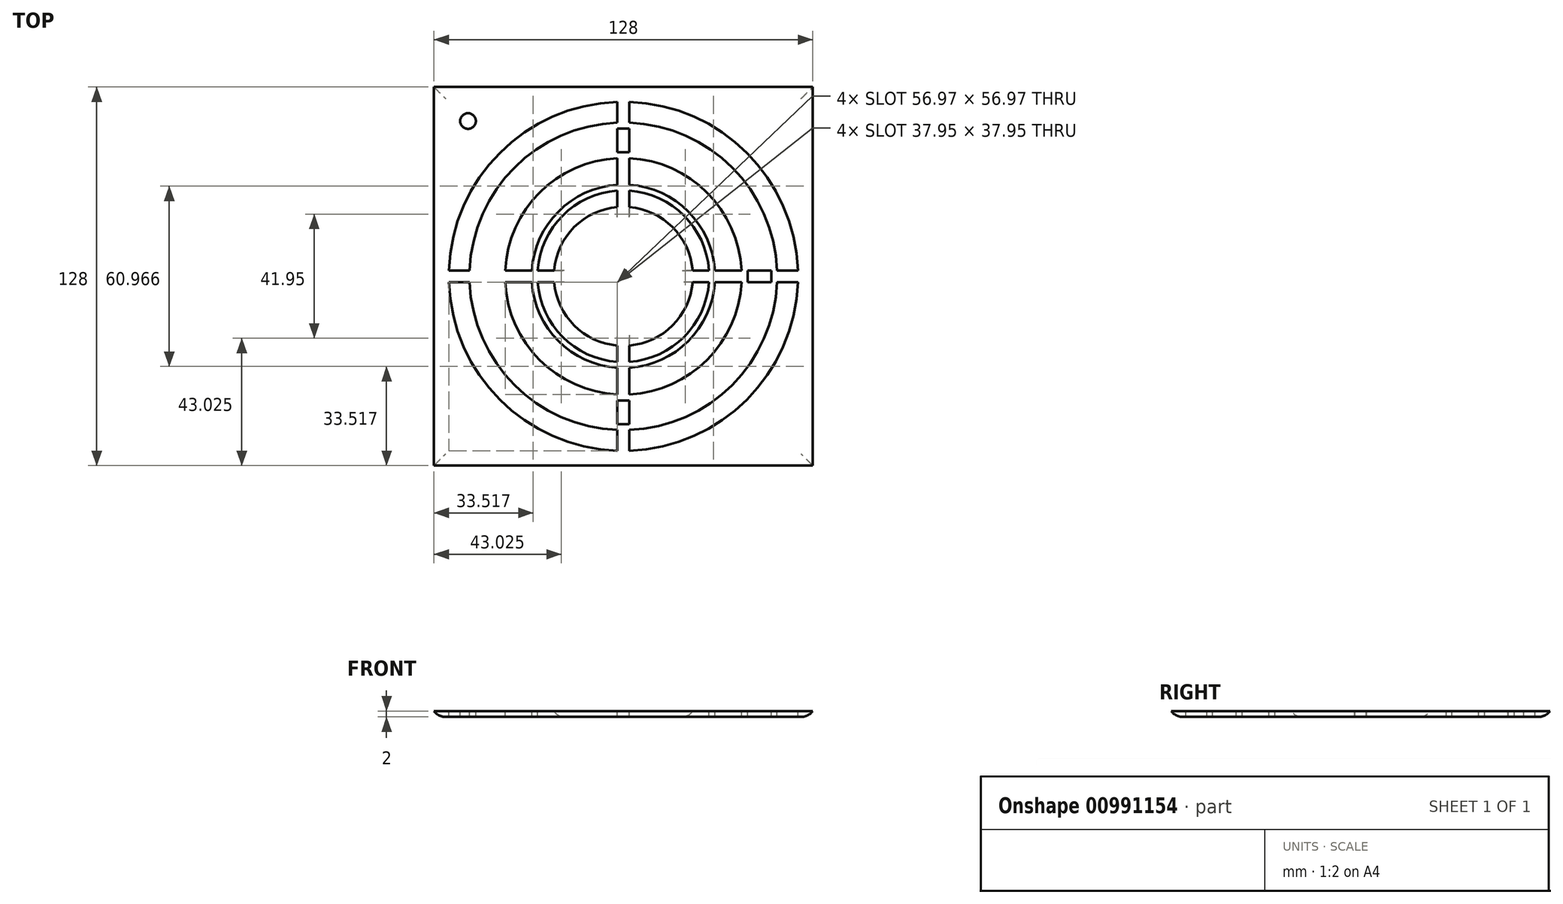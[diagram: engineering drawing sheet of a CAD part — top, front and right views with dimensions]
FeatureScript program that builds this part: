
annotation { "Feature Type Name" : "Feature", "Feature Type Description" : "" }
export const myFeature = defineFeature(function(context is Context, id is Id, definition is map)
    precondition{}
    {
        {
            var Q0;
            Q0=qCreatedBy(makeId("Top.planeOp"),FACE);
            var sketch = newSketch(context, id + "F0", { "sketchPlane" : qUnion([Q0])});
            skLineSegment(sketch, "E0.bottom", {"start": v(-64, 64) * mm, "end": v(64, 64) * mm});
            skLineSegment(sketch, "E0.top", {"start": v(-64, -64) * mm, "end": v(64, -64) * mm});
            skLineSegment(sketch, "E0.left", {"start": v(-64, 64) * mm, "end": v(-64, -64) * mm});
            skLineSegment(sketch, "E0.right", {"start": v(64, 64) * mm, "end": v(64, -64) * mm});
            skSolve(sketch);
        }
        {
            var Q0;
            Q0=makeQuery(id+"F0.imprint","IMPRINT",FACE,{"disambiguationData":[TD([[makeQuery(id+"F0.imprint","IMPRINT",EDGE,{"derivedFrom":sQuery(id+"F0.wireOp",EDGE,"E0.bottom")}),-1.0]])]});
            extrude(context, id + "F1", {"entities" : qUnion([Q0]), "depth" : 2 * mm, "offsetDistance" : 25 * mm});
        }
        {
            var Q0;
            Q0=makeQuery(id+"F1.opExtrude","CAP_FACE",FACE,{"disambiguationData":[OSD([sQuery(id+"F0.wireOp",EDGE,"E0.bottom"),sQuery(id+"F0.wireOp",EDGE,"E0.top"),sQuery(id+"F0.wireOp",EDGE,"E0.left"),sQuery(id+"F0.wireOp",EDGE,"E0.right")])],"isStart":false});
            var sketch = newSketch(context, id + "F2", { "sketchPlane" : qUnion([Q0])});
            skCircle(sketch, "E1", {"center": v(0, 0) * mm, "radius": 59 * mm});
            skCircle(sketch, "E2", {"center": v(0, 0) * mm, "radius": 23.5 * mm});
            skLineSegment(sketch, "E3", {"start": v(58.35, -64) * mm, "end": v(64, -58.35) * mm});
            skCircle(sketch, "E4", {"center": v(0, 0) * mm, "radius": 52 * mm});
            skCircle(sketch, "E5", {"center": v(0, 0) * mm, "radius": 50 * mm});
            skCircle(sketch, "E6", {"center": v(0, 0) * mm, "radius": 42 * mm});
            skCircle(sketch, "E7", {"center": v(0, 0) * mm, "radius": 40 * mm});
            skCircle(sketch, "E8", {"center": v(0, 0) * mm, "radius": 31 * mm});
            skCircle(sketch, "E9", {"center": v(0, 0) * mm, "radius": 29 * mm});
            skLineSegment(sketch, "E10.bottom", {"start": v(-2, -64) * mm, "end": v(2, -64) * mm});
            skLineSegment(sketch, "E10.top", {"start": v(-2, 64) * mm, "end": v(2, 64) * mm});
            skLineSegment(sketch, "E10.left", {"start": v(-2, -64) * mm, "end": v(-2, 64) * mm});
            skLineSegment(sketch, "E10.right", {"start": v(2, -64) * mm, "end": v(2, 64) * mm});
            skLineSegment(sketch, "E11.bottom", {"start": v(64, 2) * mm, "end": v(-64, 2) * mm});
            skLineSegment(sketch, "E11.top", {"start": v(64, -2) * mm, "end": v(-64, -2) * mm});
            skLineSegment(sketch, "E11.left", {"start": v(64, 2) * mm, "end": v(64, -2) * mm});
            skLineSegment(sketch, "E11.right", {"start": v(-64, 2) * mm, "end": v(-64, -2) * mm});
            skSolve(sketch);
        }
        {
            var Q0;
            {var subQ0=sQuery(id+"F2.wireOp",EDGE,"E10.right");var subQ1=sQuery(id+"F2.wireOp",EDGE,"E1");var subQ2=makeQuery(id+"F2.imprint","INTERSECT",VERTEX,{"disambiguationData":[OD(0.0)],"derivedFrom":[subQ1,subQ0]});Q0=makeQuery(id+"F2.imprint","IMPRINT",FACE,{"disambiguationData":[TD([[makeQuery(id+"F2.imprint","IMPRINT",EDGE,{"disambiguationData":[TD([[subQ2,1.0]])],"derivedFrom":subQ1}),1.0]])]});}
            var Q1;
            {var subQ0=sQuery(id+"F2.wireOp",EDGE,"E10.right");var subQ1=sQuery(id+"F2.wireOp",EDGE,"E5");var subQ2=makeQuery(id+"F2.imprint","INTERSECT",VERTEX,{"disambiguationData":[OD(0.0)],"derivedFrom":[subQ1,subQ0]});Q1=makeQuery(id+"F2.imprint","IMPRINT",FACE,{"disambiguationData":[TD([[makeQuery(id+"F2.imprint","IMPRINT",EDGE,{"disambiguationData":[TD([[subQ2,1.0]])],"derivedFrom":subQ1}),1.0]])]});}
            var Q2;
            {var subQ0=sQuery(id+"F2.wireOp",EDGE,"E10.right");var subQ1=sQuery(id+"F2.wireOp",EDGE,"E7");var subQ2=makeQuery(id+"F2.imprint","INTERSECT",VERTEX,{"disambiguationData":[OD(0.0)],"derivedFrom":[subQ1,subQ0]});Q2=makeQuery(id+"F2.imprint","IMPRINT",FACE,{"disambiguationData":[TD([[makeQuery(id+"F2.imprint","IMPRINT",EDGE,{"disambiguationData":[TD([[subQ2,1.0]])],"derivedFrom":subQ1}),1.0]])]});}
            var Q3;
            {var subQ0=sQuery(id+"F2.wireOp",EDGE,"E10.right");var subQ1=sQuery(id+"F2.wireOp",EDGE,"E2");var subQ2=makeQuery(id+"F2.imprint","INTERSECT",VERTEX,{"disambiguationData":[OD(0.0)],"derivedFrom":[subQ1,subQ0]});Q3=makeQuery(id+"F2.imprint","IMPRINT",FACE,{"disambiguationData":[TD([[makeQuery(id+"F2.imprint","IMPRINT",EDGE,{"disambiguationData":[TD([[subQ2,1.0]])],"derivedFrom":subQ1}),-1.0]])]});}
            var Q4;
            {var subQ0=sQuery(id+"F2.wireOp",EDGE,"E10.right");var subQ1=sQuery(id+"F2.wireOp",EDGE,"E2");var subQ2=makeQuery(id+"F2.imprint","INTERSECT",VERTEX,{"disambiguationData":[OD(1.0)],"derivedFrom":[subQ1,subQ0]});Q4=makeQuery(id+"F2.imprint","IMPRINT",FACE,{"disambiguationData":[TD([[makeQuery(id+"F2.imprint","IMPRINT",EDGE,{"disambiguationData":[TD([[subQ2,-1.0]])],"derivedFrom":subQ1}),-1.0]])]});}
            var Q5;
            {var subQ0=sQuery(id+"F2.wireOp",EDGE,"E10.right");var subQ1=sQuery(id+"F2.wireOp",EDGE,"E7");var subQ2=makeQuery(id+"F2.imprint","INTERSECT",VERTEX,{"disambiguationData":[OD(1.0)],"derivedFrom":[subQ1,subQ0]});Q5=makeQuery(id+"F2.imprint","IMPRINT",FACE,{"disambiguationData":[TD([[makeQuery(id+"F2.imprint","IMPRINT",EDGE,{"disambiguationData":[TD([[subQ2,-1.0]])],"derivedFrom":subQ1}),1.0]])]});}
            var Q6;
            {var subQ0=sQuery(id+"F2.wireOp",EDGE,"E10.right");var subQ1=sQuery(id+"F2.wireOp",EDGE,"E5");var subQ2=makeQuery(id+"F2.imprint","INTERSECT",VERTEX,{"disambiguationData":[OD(1.0)],"derivedFrom":[subQ1,subQ0]});Q6=makeQuery(id+"F2.imprint","IMPRINT",FACE,{"disambiguationData":[TD([[makeQuery(id+"F2.imprint","IMPRINT",EDGE,{"disambiguationData":[TD([[subQ2,-1.0]])],"derivedFrom":subQ1}),1.0]])]});}
            var Q7;
            {var subQ0=sQuery(id+"F2.wireOp",EDGE,"E10.right");var subQ1=sQuery(id+"F2.wireOp",EDGE,"E1");var subQ2=makeQuery(id+"F2.imprint","INTERSECT",VERTEX,{"disambiguationData":[OD(1.0)],"derivedFrom":[subQ1,subQ0]});Q7=makeQuery(id+"F2.imprint","IMPRINT",FACE,{"disambiguationData":[TD([[makeQuery(id+"F2.imprint","IMPRINT",EDGE,{"disambiguationData":[TD([[subQ2,-1.0]])],"derivedFrom":subQ1}),1.0]])]});}
            var Q8;
            {var subQ0=sQuery(id+"F2.wireOp",EDGE,"E11.top");var subQ1=sQuery(id+"F2.wireOp",EDGE,"E2");var subQ2=makeQuery(id+"F2.imprint","INTERSECT",VERTEX,{"disambiguationData":[OD(0.0)],"derivedFrom":[subQ1,subQ0]});Q8=makeQuery(id+"F2.imprint","IMPRINT",FACE,{"disambiguationData":[TD([[makeQuery(id+"F2.imprint","IMPRINT",EDGE,{"disambiguationData":[TD([[subQ2,-1.0]])],"derivedFrom":subQ1}),-1.0]])]});}
            var Q9;
            {var subQ0=sQuery(id+"F2.wireOp",EDGE,"E11.top");var subQ1=sQuery(id+"F2.wireOp",EDGE,"E7");var subQ2=makeQuery(id+"F2.imprint","INTERSECT",VERTEX,{"disambiguationData":[OD(0.0)],"derivedFrom":[subQ1,subQ0]});Q9=makeQuery(id+"F2.imprint","IMPRINT",FACE,{"disambiguationData":[TD([[makeQuery(id+"F2.imprint","IMPRINT",EDGE,{"disambiguationData":[TD([[subQ2,-1.0]])],"derivedFrom":subQ1}),1.0]])]});}
            var Q10;
            {var subQ0=sQuery(id+"F2.wireOp",EDGE,"E11.top");var subQ1=sQuery(id+"F2.wireOp",EDGE,"E5");var subQ2=makeQuery(id+"F2.imprint","INTERSECT",VERTEX,{"disambiguationData":[OD(0.0)],"derivedFrom":[subQ1,subQ0]});Q10=makeQuery(id+"F2.imprint","IMPRINT",FACE,{"disambiguationData":[TD([[makeQuery(id+"F2.imprint","IMPRINT",EDGE,{"disambiguationData":[TD([[subQ2,-1.0]])],"derivedFrom":subQ1}),1.0]])]});}
            var Q11;
            {var subQ0=sQuery(id+"F2.wireOp",EDGE,"E11.top");var subQ1=sQuery(id+"F2.wireOp",EDGE,"E1");var subQ2=makeQuery(id+"F2.imprint","INTERSECT",VERTEX,{"disambiguationData":[OD(0.0)],"derivedFrom":[subQ1,subQ0]});Q11=makeQuery(id+"F2.imprint","IMPRINT",FACE,{"disambiguationData":[TD([[makeQuery(id+"F2.imprint","IMPRINT",EDGE,{"disambiguationData":[TD([[subQ2,-1.0]])],"derivedFrom":subQ1}),1.0]])]});}
            var Q12;
            {var subQ0=sQuery(id+"F2.wireOp",EDGE,"E10.left");var subQ1=sQuery(id+"F2.wireOp",EDGE,"E2");var subQ2=makeQuery(id+"F2.imprint","INTERSECT",VERTEX,{"disambiguationData":[OD(0.0)],"derivedFrom":[subQ1,subQ0]});Q12=makeQuery(id+"F2.imprint","IMPRINT",FACE,{"disambiguationData":[TD([[makeQuery(id+"F2.imprint","IMPRINT",EDGE,{"disambiguationData":[TD([[subQ2,-1.0]])],"derivedFrom":subQ1}),-1.0]])]});}
            var Q13;
            {var subQ0=sQuery(id+"F2.wireOp",EDGE,"E10.left");var subQ1=sQuery(id+"F2.wireOp",EDGE,"E7");var subQ2=makeQuery(id+"F2.imprint","INTERSECT",VERTEX,{"disambiguationData":[OD(0.0)],"derivedFrom":[subQ1,subQ0]});Q13=makeQuery(id+"F2.imprint","IMPRINT",FACE,{"disambiguationData":[TD([[makeQuery(id+"F2.imprint","IMPRINT",EDGE,{"disambiguationData":[TD([[subQ2,-1.0]])],"derivedFrom":subQ1}),1.0]])]});}
            var Q14;
            {var subQ0=sQuery(id+"F2.wireOp",EDGE,"E10.left");var subQ1=sQuery(id+"F2.wireOp",EDGE,"E5");var subQ2=makeQuery(id+"F2.imprint","INTERSECT",VERTEX,{"disambiguationData":[OD(0.0)],"derivedFrom":[subQ1,subQ0]});Q14=makeQuery(id+"F2.imprint","IMPRINT",FACE,{"disambiguationData":[TD([[makeQuery(id+"F2.imprint","IMPRINT",EDGE,{"disambiguationData":[TD([[subQ2,-1.0]])],"derivedFrom":subQ1}),1.0]])]});}
            var Q15;
            {var subQ0=sQuery(id+"F2.wireOp",EDGE,"E10.left");var subQ1=sQuery(id+"F2.wireOp",EDGE,"E1");var subQ2=makeQuery(id+"F2.imprint","INTERSECT",VERTEX,{"disambiguationData":[OD(0.0)],"derivedFrom":[subQ1,subQ0]});Q15=makeQuery(id+"F2.imprint","IMPRINT",FACE,{"disambiguationData":[TD([[makeQuery(id+"F2.imprint","IMPRINT",EDGE,{"disambiguationData":[TD([[subQ2,-1.0]])],"derivedFrom":subQ1}),1.0]])]});}
            extrude(context, id + "F3", {"entities" : qUnion([Q0, Q1, Q2, Q3, Q4, Q5, Q6, Q7, Q8, Q9, Q10, Q11, Q12, Q13, Q14, Q15]), "operationType" : NewBodyOperationType.REMOVE, "oppositeDirection" : true, "depth" : 25 * mm, "offsetDistance" : 25 * mm});
        }
        {
            var Q0;
            Q0=makeQuery(id+"F1.opExtrude","CAP_FACE",FACE,{"disambiguationData":[OSD([sQuery(id+"F0.wireOp",EDGE,"E0.bottom"),sQuery(id+"F0.wireOp",EDGE,"E0.top"),sQuery(id+"F0.wireOp",EDGE,"E0.left"),sQuery(id+"F0.wireOp",EDGE,"E0.right")])],"isStart":false});
            var sketch = newSketch(context, id + "F4", { "sketchPlane" : qUnion([Q0])});
            skCircle(sketch, "E12", {"center": v(-52.5, 52.5) * mm, "radius": 2.65 * mm});
            skSolve(sketch);
        }
        {
            var Q0;
            Q0=makeQuery(id+"F4.imprint","IMPRINT",FACE,{"disambiguationData":[TD([[makeQuery(id+"F4.imprint","IMPRINT",EDGE,{"derivedFrom":sQuery(id+"F4.wireOp",EDGE,"E12")}),1.0]])]});
            var Q1;
            Q1=makeQuery(id+"FDiSF2rHMs3ckj9_1.1.F4.imprint","IMPRINT",FACE,{"disambiguationData":[TD([[makeQuery(id+"FDiSF2rHMs3ckj9_1.1.F4.imprint","IMPRINT",EDGE,{"derivedFrom":sQuery(id+"FDiSF2rHMs3ckj9_1.1.F4.wireOp",EDGE,"E12")}),1.0]])]});
            var Q2;
            Q2=makeQuery(id+"F1f606Lsx4S6UX4_1.1.FDiSF2rHMs3ckj9_1.1.F4.imprint","IMPRINT",FACE,{"disambiguationData":[TD([[makeQuery(id+"F1f606Lsx4S6UX4_1.1.FDiSF2rHMs3ckj9_1.1.F4.imprint","IMPRINT",EDGE,{"derivedFrom":sQuery(id+"F1f606Lsx4S6UX4_1.1.FDiSF2rHMs3ckj9_1.1.F4.wireOp",EDGE,"E12")}),1.0]])]});
            var Q3;
            Q3=makeQuery(id+"F1f606Lsx4S6UX4_1.1.F4.imprint","IMPRINT",FACE,{"disambiguationData":[TD([[makeQuery(id+"F1f606Lsx4S6UX4_1.1.F4.imprint","IMPRINT",EDGE,{"derivedFrom":sQuery(id+"F1f606Lsx4S6UX4_1.1.F4.wireOp",EDGE,"E12")}),1.0]])]});
            extrude(context, id + "F5", {"entities" : qUnion([Q0, Q1, Q2, Q3]), "operationType" : NewBodyOperationType.REMOVE, "oppositeDirection" : true, "depth" : 25 * mm, "offsetDistance" : 25 * mm});
        }
        {
            var Q0;
            Q0=makeQuery(id+"F1.opExtrude","CAP_EDGE",EDGE,{"disambiguationData":[OSD([sQuery(id+"F0.wireOp",EDGE,"E0.top")])],"isStart":true});
            var Q1;
            Q1=makeQuery(id+"F1.opExtrude","CAP_EDGE",EDGE,{"disambiguationData":[OSD([sQuery(id+"F0.wireOp",EDGE,"E0.left")])],"isStart":true});
            var Q2;
            Q2=makeQuery(id+"F1.opExtrude","CAP_EDGE",EDGE,{"disambiguationData":[OSD([sQuery(id+"F0.wireOp",EDGE,"E0.bottom")])],"isStart":true});
            var Q3;
            Q3=makeQuery(id+"F1.opExtrude","CAP_EDGE",EDGE,{"disambiguationData":[OSD([sQuery(id+"F0.wireOp",EDGE,"E0.right")])],"isStart":true});
            fillet(context, id + "F6", {"entities" : qUnion([Q0, Q1, Q2, Q3]), "radius" : 5 * mm, "tangentPropagation" : true, "allowEdgeOverflow" : false});
        }
        {
            var Q0;
            {var subQ0=sQuery(id+"F2.wireOp",EDGE,"E2");Q0=makeQuery(id+"F3.boolean.opBoolean","INTERSECT",EDGE,{"derivedFrom":[makeQuery(id+"F1.opExtrude","CAP_FACE",FACE,{"disambiguationData":[OSD([sQuery(id+"F0.wireOp",EDGE,"E0.bottom"),sQuery(id+"F0.wireOp",EDGE,"E0.top"),sQuery(id+"F0.wireOp",EDGE,"E0.left"),sQuery(id+"F0.wireOp",EDGE,"E0.right")])],"isStart":true}),makeQuery(id+"F3.opExtrude","SWEPT_FACE",FACE,{"disambiguationData":[OSD([subQ0]),TDD([makeQuery(id+"F2.imprint","IMPRINT",EDGE,{"disambiguationData":[TD([[makeQuery(id+"F2.imprint","INTERSECT",VERTEX,{"disambiguationData":[OD(0.0)],"derivedFrom":[subQ0,sQuery(id+"F2.wireOp",EDGE,"E10.left")]}),-1.0]])],"derivedFrom":subQ0})])]})]});}
            var Q1;
            {var subQ0=sQuery(id+"F2.wireOp",EDGE,"E2");Q1=makeQuery(id+"F3.boolean.opBoolean","INTERSECT",EDGE,{"derivedFrom":[makeQuery(id+"F1.opExtrude","CAP_FACE",FACE,{"disambiguationData":[OSD([sQuery(id+"F0.wireOp",EDGE,"E0.bottom"),sQuery(id+"F0.wireOp",EDGE,"E0.top"),sQuery(id+"F0.wireOp",EDGE,"E0.left"),sQuery(id+"F0.wireOp",EDGE,"E0.right")])],"isStart":true}),makeQuery(id+"F3.opExtrude","SWEPT_FACE",FACE,{"disambiguationData":[OSD([subQ0]),TDD([makeQuery(id+"F2.imprint","IMPRINT",EDGE,{"disambiguationData":[TD([[makeQuery(id+"F2.imprint","INTERSECT",VERTEX,{"disambiguationData":[OD(0.0)],"derivedFrom":[subQ0,sQuery(id+"F2.wireOp",EDGE,"E10.right")]}),1.0]])],"derivedFrom":subQ0})])]})]});}
            var Q2;
            {var subQ0=sQuery(id+"F2.wireOp",EDGE,"E2");Q2=makeQuery(id+"F3.boolean.opBoolean","INTERSECT",EDGE,{"derivedFrom":[makeQuery(id+"F1.opExtrude","CAP_FACE",FACE,{"disambiguationData":[OSD([sQuery(id+"F0.wireOp",EDGE,"E0.bottom"),sQuery(id+"F0.wireOp",EDGE,"E0.top"),sQuery(id+"F0.wireOp",EDGE,"E0.left"),sQuery(id+"F0.wireOp",EDGE,"E0.right")])],"isStart":true}),makeQuery(id+"F3.opExtrude","SWEPT_FACE",FACE,{"disambiguationData":[OSD([subQ0]),TDD([makeQuery(id+"F2.imprint","IMPRINT",EDGE,{"disambiguationData":[TD([[makeQuery(id+"F2.imprint","INTERSECT",VERTEX,{"disambiguationData":[OD(1.0)],"derivedFrom":[subQ0,sQuery(id+"F2.wireOp",EDGE,"E10.right")]}),-1.0]])],"derivedFrom":subQ0})])]})]});}
            var Q3;
            {var subQ0=sQuery(id+"F2.wireOp",EDGE,"E2");Q3=makeQuery(id+"F3.boolean.opBoolean","INTERSECT",EDGE,{"derivedFrom":[makeQuery(id+"F1.opExtrude","CAP_FACE",FACE,{"disambiguationData":[OSD([sQuery(id+"F0.wireOp",EDGE,"E0.bottom"),sQuery(id+"F0.wireOp",EDGE,"E0.top"),sQuery(id+"F0.wireOp",EDGE,"E0.left"),sQuery(id+"F0.wireOp",EDGE,"E0.right")])],"isStart":true}),makeQuery(id+"F3.opExtrude","SWEPT_FACE",FACE,{"disambiguationData":[OSD([subQ0]),TDD([makeQuery(id+"F2.imprint","IMPRINT",EDGE,{"disambiguationData":[TD([[makeQuery(id+"F2.imprint","INTERSECT",VERTEX,{"disambiguationData":[OD(0.0)],"derivedFrom":[subQ0,sQuery(id+"F2.wireOp",EDGE,"E11.top")]}),-1.0]])],"derivedFrom":subQ0})])]})]});}
            fillet(context, id + "F7", {"entities" : qUnion([Q0, Q1, Q2, Q3]), "radius" : 4 * mm, "tangentPropagation" : true, "allowEdgeOverflow" : false});
        }
    });
